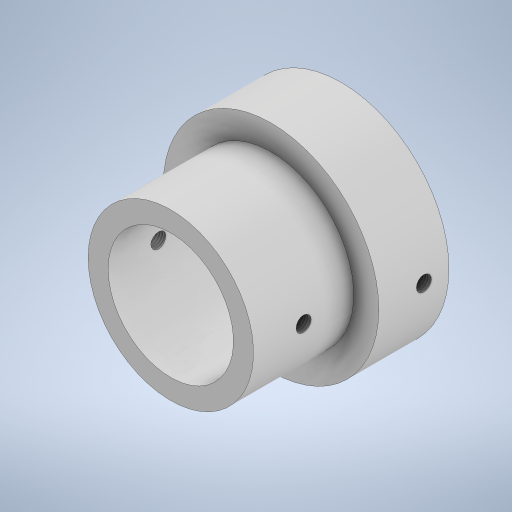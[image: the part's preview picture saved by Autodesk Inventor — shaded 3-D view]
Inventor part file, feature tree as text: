
AUTODESK INVENTOR PART (.ipt)
format: ipt  version: 2023 (Build 270158000, 158)  size: 291,328 bytes
history: native  units: mm
features: thread x2, sketch x2, other x1, revolve x1, extrude x1
ambient origin geometry x8: Origin, YZ Plane, XZ Plane, XY Plane, X Axis, Y Axis, Z Axis, Center Point
bodies: Body1 (feature_tree)
feature tree (7):
  other  "Твердое тело1"
  revolve  "Вращение1"
  extrude  "Выдавливание1"  Depth=12.5mm
  thread  "Резьба1"
  thread  "Резьба2"
  sketch  "Эскиз1"
  sketch  "Эскиз2"
